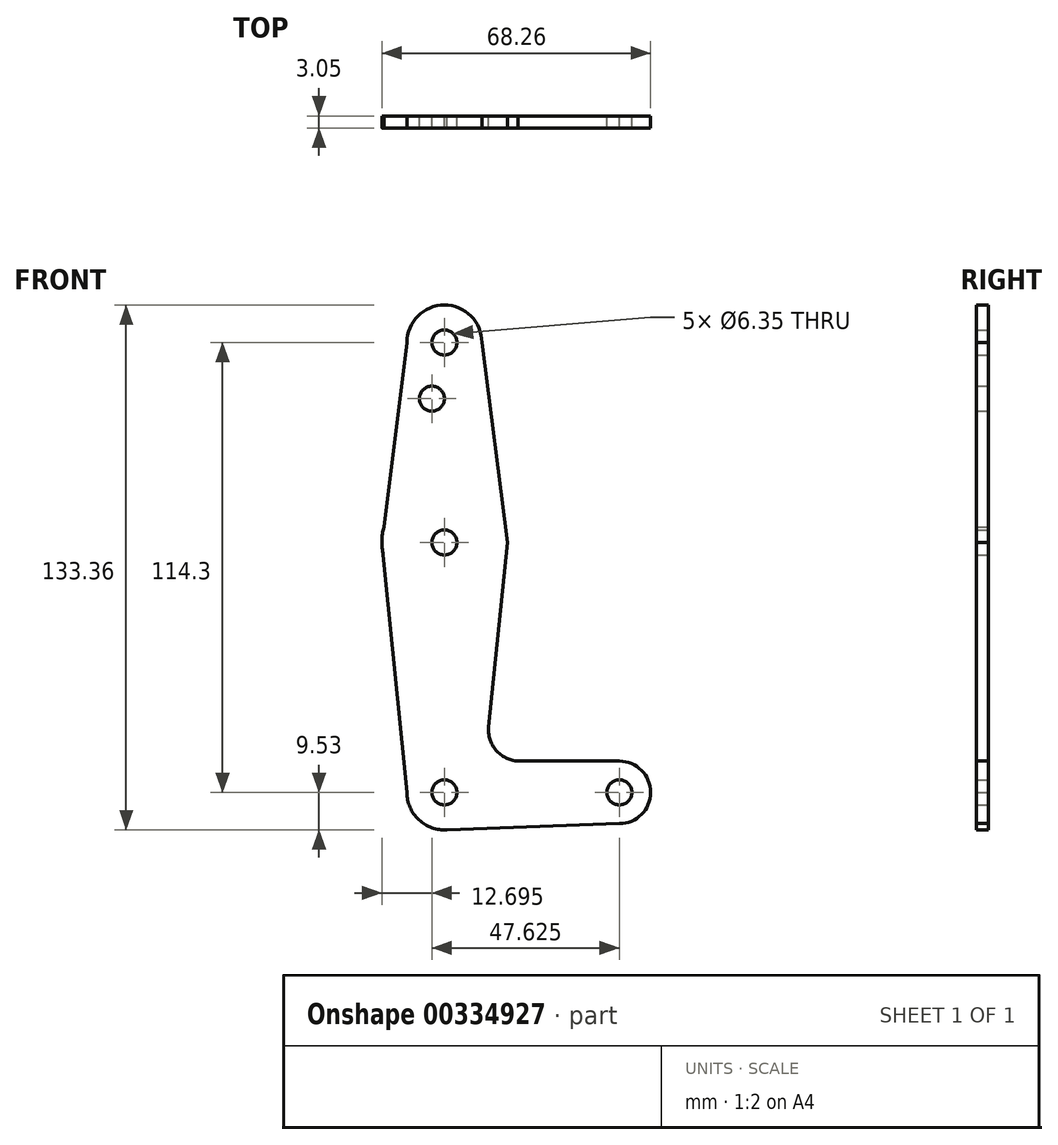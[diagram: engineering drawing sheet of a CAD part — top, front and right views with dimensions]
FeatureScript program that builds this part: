
annotation { "Feature Type Name" : "Feature", "Feature Type Description" : "" }
export const myFeature = defineFeature(function(context is Context, id is Id, definition is map)
    precondition{}
    {
        {
            var Q0;
            Q0=qCreatedBy(makeId("Front.planeOp"),FACE);
            var sketch = newSketch(context, id + "F0", { "sketchPlane" : qUnion([Q0])});
            skLineSegment(sketch, "E0", {"start": v(0, 114.3) * mm, "end": v(0, 0) * mm, "construction": true});
            skLineSegment(sketch, "E1", {"start": v(0, 0) * mm, "end": v(44.45, 0) * mm, "construction": true});
            skCircle(sketch, "E2", {"center": v(0, 114.3) * mm, "radius": 9.53 * mm});
            skCircle(sketch, "E3", {"center": v(0, 63.5) * mm, "radius": 15.88 * mm});
            skCircle(sketch, "E4", {"center": v(0, 0) * mm, "radius": 9.53 * mm});
            skCircle(sketch, "E5", {"center": v(44.45, 0) * mm, "radius": 7.94 * mm});
            skLineSegment(sketch, "E6", {"start": v(-9.53, 114.3) * mm, "end": v(-15.88, 63.5) * mm});
            skLineSegment(sketch, "E7", {"start": v(9.52, 114.3) * mm, "end": v(16, 63.5) * mm});
            skLineSegment(sketch, "E8", {"start": v(-15.88, 63.5) * mm, "end": v(-9.53, 0) * mm});
            skLineSegment(sketch, "E9", {"start": v(16, 63.5) * mm, "end": v(11.26, 16.67) * mm});
            skLineSegment(sketch, "E10", {"start": v(0, -9.52) * mm, "end": v(44.45, -7.94) * mm});
            skCircle(sketch, "E11", {"center": v(0, 114.3) * mm, "radius": 3.18 * mm});
            skCircle(sketch, "E12", {"center": v(0, 0) * mm, "radius": 3.18 * mm});
            skCircle(sketch, "E13", {"center": v(0, 63.5) * mm, "radius": 3.18 * mm});
            skCircle(sketch, "E14", {"center": v(44.45, 0) * mm, "radius": 3.18 * mm});
            skCircle(sketch, "E15", {"center": v(-3.18, 100.03) * mm, "radius": 3.18 * mm});
            skArc(sketch, "E16.filletArc", {"start": v(11.26, 16.67) * mm, "mid": v(13.11, 10.73) * mm, "end": v(18.68, 7.94) * mm});
            skLineSegment(sketch, "E17", {"start": v(18.68, 7.94) * mm, "end": v(44.45, 7.94) * mm});
            skSolve(sketch);
        }
        {
            var Q0;
            Q0 = qSketchRegion(id + "F0", true);
            extrude(context, id + "F1", {"entities" : qUnion([Q0]), "depth" : 3.05 * mm});
        }
    });
